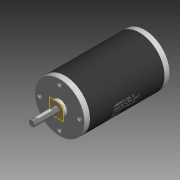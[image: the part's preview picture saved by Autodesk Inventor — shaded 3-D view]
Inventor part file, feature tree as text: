
AUTODESK INVENTOR PART (.ipt)
format: ipt  version: 2018 (Build 220112000, 112)  size: 7,094,784 bytes
history: native  units: mm (DEFAULTED — no unit token found)
features: sketch x10, extrude x7, chamfer x4, plane x3, hole x2, pattern_circular x2, fillet x2, emboss x1, split x1
ambient origin geometry x8: Origin, YZ Plane, XZ Plane, XY Plane, X Axis, Y Axis, Z Axis, Center Point
bodies: Solid1 (feature_tree), Solid2 (feature_tree), Solid3 (feature_tree)
feature tree (32):
  extrude  "Extrusion1"  Depth=7.0mm TaperAngle=0.0deg
  extrude  "Extrusion2"  Depth=3.9878mm TaperAngle=0.0deg
  chamfer  "Chamfer1"  Distance=1.0mm
  hole  "Hole2"  [1 undecoded]
  pattern_circular  "Circular Pattern2"  Count=4 Angle=90.0deg
  chamfer  "Chamfer3"  Distance=31.623mm
  extrude  "Extrusion3"  Depth=12.7mm
  fillet  "Fillet1"  Radius=64.4144mm
  extrude  "Extrusion5"  Depth=64.008mm
  extrude  "Extrusion6"  Depth=7.0mm
  extrude  "Extrusion7"  Depth=0.508mm
  hole  "Hole3"  [1 undecoded]
  chamfer  "Chamfer2"  Distance=20.0mm Angle=360.0deg
  pattern_circular  "Circular Pattern3"  [2 undecoded]
  fillet  "Fillet2"  [1 undecoded]
  chamfer  "Chamfer4"  Distance=1.99898mm
  plane  "Work Plane1"
  extrude  "Extrusion8"  Depth=1.99898mm
  plane  "Work Plane2"
  emboss  "Emboss1"
  plane  "Work Plane3"
  split  "Split1"
  sketch  "Sketch1"  dims[d0=64.008mm d1=7.0mm d2=0.0mm]
  sketch  "Sketch2"  dims[d3=19.05mm d4=3.9878mm d5=0.0mm d6=1.0mm d7=1.0mm]
  sketch  "Sketch4"  dims[d18=3.9624mm d19=9.525mm d20=6.35mm d21=60.0deg d22=19.05mm d23=20.594885mm d24=25.4mm d25=40.0mm d27=90.0deg]
  sketch  "Sketch5"  dims[d28=7.9502mm d29=31.623mm d30=0.0mm]
  sketch  "Sketch8"  dims[d31=0.79375mm d33=12.7mm d38=64.4144mm]
  sketch  "Sketch9"  dims[d39=95.6056mm d40=0.0mm d41=64.008mm]
  sketch  "Sketch10"  dims[d42=7.0mm d43=0.0mm d44=30.1498mm]
  sketch  "Sketch11"  dims[d45=4.1148mm d46=0.0mm]
  sketch  "Sketch12"  dims[d47=5.08mm d48=12.7mm d49=9.906mm d50=4.572mm d51=14.3117mm d52=7.62mm d53=20.594885mm d54=0.508mm d55=3.175mm]
  sketch  "Sketch13"  dims[d56=0.762mm d57=0.762mm d58=3.175mm d59=20.0mm d61=360.0deg d62=0.25mm d63=3.175mm d64=45.0deg d65=45.0deg d66=45.0deg d67=45.0deg d68=1.99898mm d70=20.09902mm d71=7.99338mm d72=1.15062mm d73=0.0mm d74=30.48mm d75=0.0254mm d76=0.0mm d77=0.0mm]
note: 5 required parameter values undecoded (feature->parameter linkage not recoverable at this tier; creation-order binding heuristic only, values carry confidence <= 0.55)
